# Revit family: PRD_FrankeWS_HndDrrs_STRATOSElectronicHandDryer_STRX220
name_source: partatom
category: Specialty Equipment
revit_build: Autodesk Revit 2018 (Build: 20190510_1515(x64)
units: mm (PartAtom-declared; Revit-internal decimal feet)

## family parameters
Cut with Voids When Loaded = No
Host = Face
OmniClass Number = 23.40.20.21.14
OmniClass Title = Hand and Hair Dryers
Part Type = Normal
Room Calculation Point = No
Round Connector Dimension = Use Diameter
Shared = No

## types (1)
- STRX220
    AirVelocity = Adjustable, 95-115 m/s
    AirVolume = 80.0 m³/h
    AssetType = Fixed
    BIMObjectName = PRD_AR_HndDrrs_STRATOSElectronicHandDryer_STRX220
    Category = Pr_40_70_62_37, Hand dryers
    ConnectionVoltage = 230-240 V, 50-60 Hz
    Default Elevation = 850 mm  [stored 2.78871 ft]
    Description = Touch free electronic warm air hand dryer for wall mounting, stainless steel, surface satin finished, front with InoxPlus surface refinement for the reduction of finger marks and better cleaning characteristics (easy to clean), material thickness 1.5mm, curved front cover, infra-red sensor activity for non-touch operation, adjustable warm air temperature, sensor range adjustable from 10 to 25 cm, automatic power shut-off after 60 seconds, adjustable air velocity allows to shorten the drying time considerably, cable and plug not included.
    DurationUnit = year
    Features = Stainless steel, surface satin finished
    Finish = satin finished
    GrossWeight = 4.50 kg
    HandDryerMaterial = PRD_AR_StainlessSteel_SatinFinished
    HeatingPower = 500 W
    IP_Code = IPX1
    IfcExportAs = IfcElectricApplianceType
    IfcExportType = HANDDRYER
    InputSupplyVoltageHz = 50 Hz
    InputSupplyVoltageV = 220 V
    IntegralAccessories = cable and plug not included
    LoadClassification = Other
    Manufacturer = KWC Group AG
    ManufacturerName = KWC Group AG
    ManufacturerURL = www.kwc.com
    Material = Stainless steel
    MaterialCode = 1.4301
    MaterialThickness = 1.50 mm
    Model = STRX220
    ModelNumber = 2030027296
    ModelReference = STRX220
    MotorPower = 500 W
    NBSDescription = Hand dryers
    NBSReference = 45-35-72/334
    Name = STRATOS Electronic Hand Dryer STRX220
    NetWeight = 4.30 kg
    NominalDepth = 130 mm  [stored 0.426509 ft]
    NominalFrequencyRange = 50-60 Hz
    NominalHeight = 267 mm  [stored 0.875984 ft]
    NominalWidth = 156 mm  [stored 0.511811 ft]
    PowerFactor = 1
    ProductInformation = https://pim.kwc.com
    RatedCurrent = 0
    RatedVoltage = 230-240 V
    Size = 156 x 267 x 130 mm
    SoundLevel = 76.20 dB
    SurfaceTreatment = InoxPlus (anti fingerprint)
    TotalPower = 1000 W
    TypeOfFixing = Screw
    TypeOfMounting = Wall mounting
    TypeOfOperation = Sensor operation
    URL = www.kwc.com
    Uniclass2015Code = Pr_40_70_62_37
    Uniclass2015Title = Hand dryers
    Uniclass2015Version = Products v1.10
    Version = 1
    Voltage = 240 V
    WarrantyDurationUnit = year

note: [stored X ft] marks values corroborated as IEEE doubles in the binary element streams (Revit-internal decimal feet)

## geometry (parser evidence)
native form markers: Sweep x5
no freeform markers — native parametric forms only
